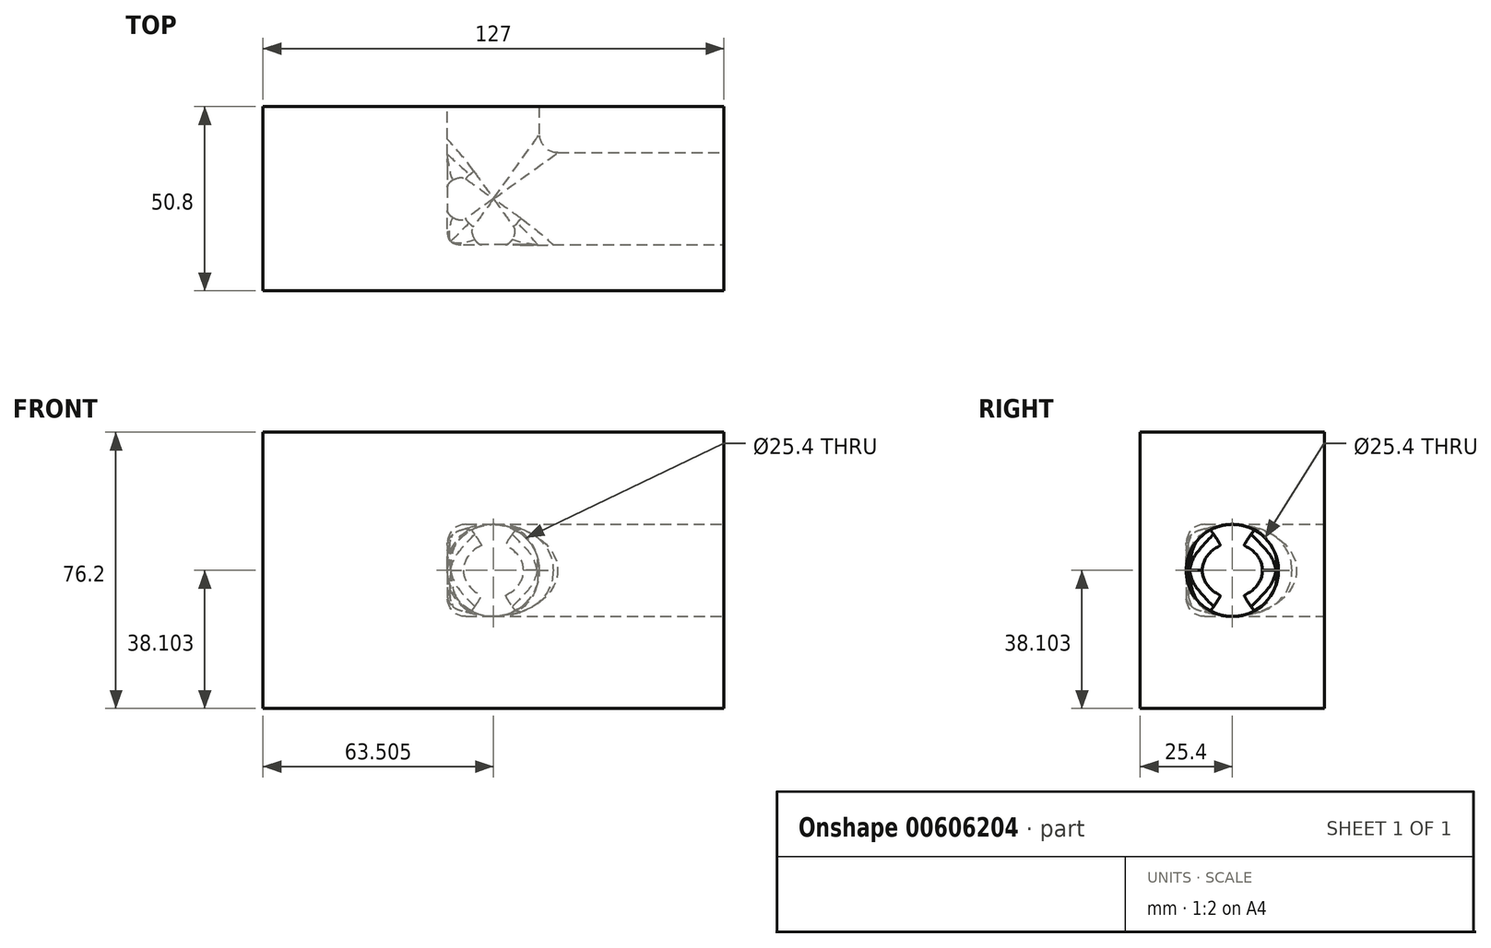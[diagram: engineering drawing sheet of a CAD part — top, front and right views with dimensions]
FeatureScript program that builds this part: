
annotation { "Feature Type Name" : "Feature", "Feature Type Description" : "" }
export const myFeature = defineFeature(function(context is Context, id is Id, definition is map)
    precondition{}
    {
        {
            var Q0;
            Q0=qCreatedBy(makeId("Front.planeOp"),FACE);
            var sketch = newSketch(context, id + "F0", { "sketchPlane" : qUnion([Q0])});
            skLineSegment(sketch, "E0.bottom", {"start": v(-62.25, 38.85) * mm, "end": v(64.75, 38.85) * mm});
            skLineSegment(sketch, "E0.top", {"start": v(-62.25, -37.35) * mm, "end": v(64.75, -37.35) * mm});
            skLineSegment(sketch, "E0.left", {"start": v(-62.25, 38.85) * mm, "end": v(-62.25, -37.35) * mm});
            skLineSegment(sketch, "E0.right", {"start": v(64.75, 38.85) * mm, "end": v(64.75, -37.35) * mm});
            skSolve(sketch);
        }
        {
            var Q0;
            Q0=makeQuery(id+"F0.imprint","IMPRINT",FACE,{"disambiguationData":[TD([[makeQuery(id+"F0.imprint","IMPRINT",EDGE,{"derivedFrom":sQuery(id+"F0.wireOp",EDGE,"E0.bottom")}),-1.0]])]});
            extrude(context, id + "F1", {"entities" : qUnion([Q0]), "depth" : 50.8 * mm, "offsetDistance" : 25.4 * mm});
        }
        {
            var Q0;
            Q0=qCreatedBy(makeId("Front.planeOp"),FACE);
            var sketch = newSketch(context, id + "F2", { "sketchPlane" : qUnion([Q0])});
            skCircle(sketch, "E1", {"center": v(1.25, 0.75) * mm, "radius": 12.7 * mm});
            skSolve(sketch);
        }
        {
            var Q0;
            Q0 = qSketchRegion(id + "F2", true);
            extrude(context, id + "F3", {"entities" : qUnion([Q0]), "operationType" : NewBodyOperationType.REMOVE, "depth" : 38.1 * mm, "offsetDistance" : 25.4 * mm});
        }
        {
            var Q0;
            Q0=makeQuery(id+"F1.opExtrude","SWEPT_FACE",FACE,{"disambiguationData":[OSD([sQuery(id+"F0.wireOp",EDGE,"E0.right")])]});
            var sketch = newSketch(context, id + "F4", { "sketchPlane" : qUnion([Q0])});
            skCircle(sketch, "E2", {"center": v(-25.4, 0.75) * mm, "radius": 12.7 * mm});
            skSolve(sketch);
        }
        {
            var Q0;
            Q0 = qSketchRegion(id + "F4", true);
            extrude(context, id + "F5", {"entities" : qUnion([Q0]), "operationType" : NewBodyOperationType.REMOVE, "oppositeDirection" : true, "depth" : 76.2 * mm, "offsetDistance" : 25.4 * mm});
        }
        {
            var Q0;
            Q0=makeQuery(id+"F5.boolean.opBoolean","INTERSECT",EDGE,{"disambiguationData":[OD(6.0)],"derivedFrom":[makeQuery(id+"F3.boolean.opBoolean","COPY",FACE,{"derivedFrom":makeQuery(id+"F3.opExtrude","SWEPT_FACE",FACE,{"disambiguationData":[OSD([sQuery(id+"F2.wireOp",EDGE,"E1")])]})}),makeQuery(id+"F5.opExtrude","SWEPT_FACE",FACE,{"disambiguationData":[OSD([sQuery(id+"F4.wireOp",EDGE,"E2")])]})]});
            var Q1;
            Q1=makeQuery(id+"F5.boolean.opBoolean","COPY",EDGE,{"disambiguationData":[OD(1.0)],"derivedFrom":makeQuery(id+"F5.opExtrude","CAP_EDGE",EDGE,{"disambiguationData":[OSD([sQuery(id+"F4.wireOp",EDGE,"E2")])],"isStart":false})});
            var Q2;
            Q2=makeQuery(id+"F5.boolean.opBoolean","SPLIT",EDGE,{"disambiguationData":[OD(1.0)],"derivedFrom":makeQuery(id+"F3.boolean.opBoolean","COPY",EDGE,{"derivedFrom":makeQuery(id+"F3.opExtrude","CAP_EDGE",EDGE,{"disambiguationData":[OSD([sQuery(id+"F2.wireOp",EDGE,"E1")])],"isStart":false})})});
            var Q3;
            Q3=makeQuery(id+"F5.boolean.opBoolean","COPY",EDGE,{"disambiguationData":[OD(0.0)],"derivedFrom":makeQuery(id+"F5.opExtrude","CAP_EDGE",EDGE,{"disambiguationData":[OSD([sQuery(id+"F4.wireOp",EDGE,"E2")])],"isStart":false})});
            var Q4;
            Q4=makeQuery(id+"F5.boolean.opBoolean","INTERSECT",EDGE,{"disambiguationData":[OD(5.0)],"derivedFrom":[makeQuery(id+"F3.boolean.opBoolean","COPY",FACE,{"derivedFrom":makeQuery(id+"F3.opExtrude","SWEPT_FACE",FACE,{"disambiguationData":[OSD([sQuery(id+"F2.wireOp",EDGE,"E1")])]})}),makeQuery(id+"F5.opExtrude","SWEPT_FACE",FACE,{"disambiguationData":[OSD([sQuery(id+"F4.wireOp",EDGE,"E2")])]})]});
            var Q5;
            Q5=makeQuery(id+"F5.boolean.opBoolean","SPLIT",EDGE,{"disambiguationData":[OD(0.0)],"derivedFrom":makeQuery(id+"F3.boolean.opBoolean","COPY",EDGE,{"derivedFrom":makeQuery(id+"F3.opExtrude","CAP_EDGE",EDGE,{"disambiguationData":[OSD([sQuery(id+"F2.wireOp",EDGE,"E1")])],"isStart":false})})});
            var Q6;
            Q6=makeQuery(id+"F5.boolean.opBoolean","INTERSECT",EDGE,{"disambiguationData":[OD(4.0)],"derivedFrom":[makeQuery(id+"F3.boolean.opBoolean","COPY",FACE,{"derivedFrom":makeQuery(id+"F3.opExtrude","SWEPT_FACE",FACE,{"disambiguationData":[OSD([sQuery(id+"F2.wireOp",EDGE,"E1")])]})}),makeQuery(id+"F5.opExtrude","SWEPT_FACE",FACE,{"disambiguationData":[OSD([sQuery(id+"F4.wireOp",EDGE,"E2")])]})]});
            var Q7;
            Q7=makeQuery(id+"F5.boolean.opBoolean","INTERSECT",EDGE,{"disambiguationData":[OD(3.0)],"derivedFrom":[makeQuery(id+"F3.boolean.opBoolean","COPY",FACE,{"derivedFrom":makeQuery(id+"F3.opExtrude","SWEPT_FACE",FACE,{"disambiguationData":[OSD([sQuery(id+"F2.wireOp",EDGE,"E1")])]})}),makeQuery(id+"F5.opExtrude","SWEPT_FACE",FACE,{"disambiguationData":[OSD([sQuery(id+"F4.wireOp",EDGE,"E2")])]})]});
            var Q8;
            Q8=makeQuery(id+"F5.boolean.opBoolean","INTERSECT",EDGE,{"disambiguationData":[OD(2.0)],"derivedFrom":[makeQuery(id+"F3.boolean.opBoolean","COPY",FACE,{"derivedFrom":makeQuery(id+"F3.opExtrude","SWEPT_FACE",FACE,{"disambiguationData":[OSD([sQuery(id+"F2.wireOp",EDGE,"E1")])]})}),makeQuery(id+"F5.opExtrude","SWEPT_FACE",FACE,{"disambiguationData":[OSD([sQuery(id+"F4.wireOp",EDGE,"E2")])]})]});
            var Q9;
            Q9=makeQuery(id+"F5.boolean.opBoolean","INTERSECT",EDGE,{"disambiguationData":[OD(1.0)],"derivedFrom":[makeQuery(id+"F3.boolean.opBoolean","COPY",FACE,{"derivedFrom":makeQuery(id+"F3.opExtrude","SWEPT_FACE",FACE,{"disambiguationData":[OSD([sQuery(id+"F2.wireOp",EDGE,"E1")])]})}),makeQuery(id+"F5.opExtrude","SWEPT_FACE",FACE,{"disambiguationData":[OSD([sQuery(id+"F4.wireOp",EDGE,"E2")])]})]});
            var Q10;
            Q10=makeQuery(id+"F5.boolean.opBoolean","INTERSECT",EDGE,{"disambiguationData":[OD(0.0)],"derivedFrom":[makeQuery(id+"F3.boolean.opBoolean","COPY",FACE,{"derivedFrom":makeQuery(id+"F3.opExtrude","SWEPT_FACE",FACE,{"disambiguationData":[OSD([sQuery(id+"F2.wireOp",EDGE,"E1")])]})}),makeQuery(id+"F5.opExtrude","SWEPT_FACE",FACE,{"disambiguationData":[OSD([sQuery(id+"F4.wireOp",EDGE,"E2")])]})]});
            fillet(context, id + "F6", {"entities" : qUnion([Q0, Q1, Q2, Q3, Q4, Q5, Q6, Q7, Q8, Q9, Q10]), "radius" : 5.08 * mm, "tangentPropagation" : true, "allowEdgeOverflow" : false});
        }
    });
